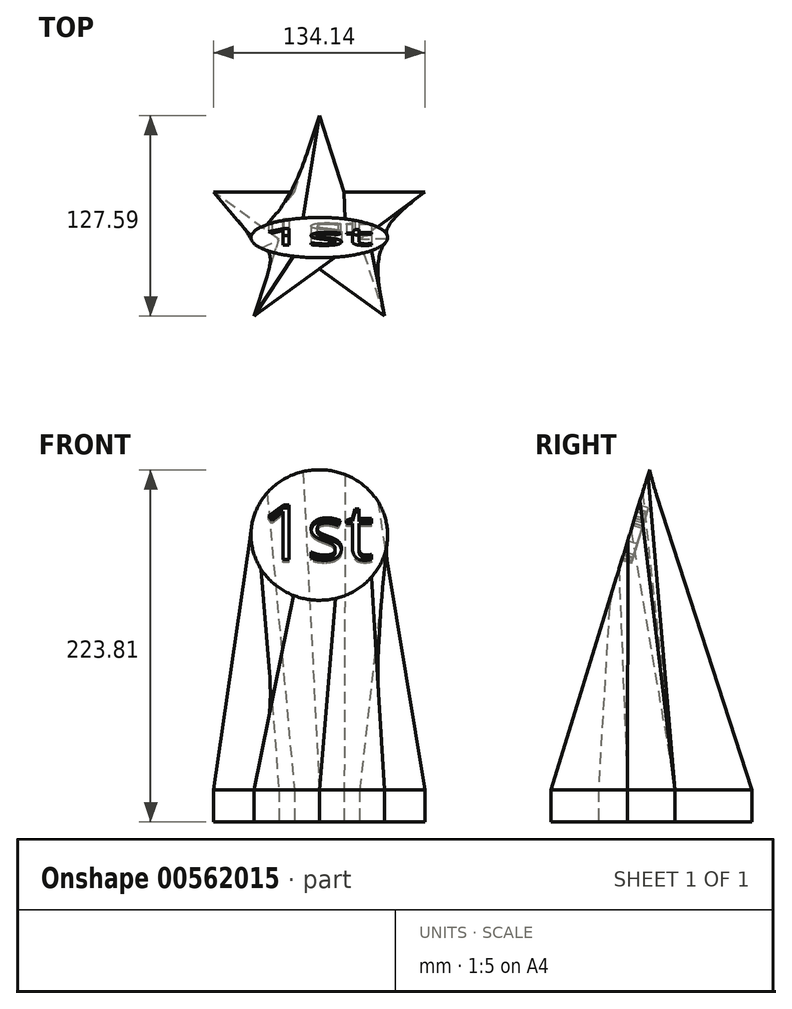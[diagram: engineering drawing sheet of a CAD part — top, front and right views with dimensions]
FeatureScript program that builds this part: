
annotation { "Feature Type Name" : "Feature", "Feature Type Description" : "" }
export const myFeature = defineFeature(function(context is Context, id is Id, definition is map)
    precondition{}
    {
        {
            var Q0;
            Q0=qCreatedBy(makeId("Top.planeOp"),FACE);
            var sketch = newSketch(context, id + "F0", { "sketchPlane" : qUnion([Q0])});
            skPoint(sketch, "E0.0.midPoint", {"position": v(-33.54, 46.16) * mm});
            skLineSegment(sketch, "E1", {"start": v(41.45, -57.06) * mm, "end": v(0, -26.94) * mm});
            skLineSegment(sketch, "E2", {"start": v(67.07, 21.8) * mm, "end": v(25.62, -8.32) * mm});
            skLineSegment(sketch, "E3", {"start": v(-41.45, -57.06) * mm, "end": v(-25.62, -8.32) * mm});
            skLineSegment(sketch, "E4", {"start": v(41.45, -57.06) * mm, "end": v(25.62, -8.32) * mm});
            skLineSegment(sketch, "E5", {"start": v(67.07, 21.8) * mm, "end": v(15.83, 21.8) * mm});
            skLineSegment(sketch, "E6.trimOffspring", {"start": v(-15.83, 21.8) * mm, "end": v(0, 70.53) * mm});
            skLineSegment(sketch, "E7.trimOffspring", {"start": v(-15.83, 21.8) * mm, "end": v(-67.07, 21.8) * mm});
            skLineSegment(sketch, "E8.trimOffspring", {"start": v(15.83, 21.8) * mm, "end": v(0, 70.53) * mm});
            skLineSegment(sketch, "E9.trimOffspring", {"start": v(0, -26.94) * mm, "end": v(-41.45, -57.06) * mm});
            skLineSegment(sketch, "E10.trimOffspring", {"start": v(-25.62, -8.32) * mm, "end": v(-67.07, 21.8) * mm});
            skLineSegment(sketch, "E11", {"start": v(-41.45, -57.06) * mm, "end": v(41.45, -57.06) * mm});
            skSolve(sketch);
        }
        {
            var Q0;
            Q0=makeQuery(id+"F0.imprint","IMPRINT",FACE,{"disambiguationData":[TD([[makeQuery(id+"F0.imprint","IMPRINT",EDGE,{"derivedFrom":sQuery(id+"F0.wireOp",EDGE,"E1")}),-1.0]])]});
            extrude(context, id + "F1", {"entities" : qUnion([Q0]), "depth" : 20.32 * mm, "offsetDistance" : 25.4 * mm});
        }
        {
            var Q0;
            Q0=makeQuery(id+"F1.opExtrude","CAP_FACE",FACE,{"disambiguationData":[OSD([sQuery(id+"F0.wireOp",EDGE,"E1"),sQuery(id+"F0.wireOp",EDGE,"E2"),sQuery(id+"F0.wireOp",EDGE,"E3"),sQuery(id+"F0.wireOp",EDGE,"E4"),sQuery(id+"F0.wireOp",EDGE,"E5"),sQuery(id+"F0.wireOp",EDGE,"E6.trimOffspring"),sQuery(id+"F0.wireOp",EDGE,"E7.trimOffspring"),sQuery(id+"F0.wireOp",EDGE,"E8.trimOffspring"),sQuery(id+"F0.wireOp",EDGE,"E9.trimOffspring"),sQuery(id+"F0.wireOp",EDGE,"E10.trimOffspring")])],"isStart":false});
            var sketch = newSketch(context, id + "F2", { "sketchPlane" : qUnion([Q0])});
            skLineSegment(sketch, "E12.0", {"start": v(-41.45, -57.06) * mm, "end": v(41.45, -57.06) * mm});
            skSolve(sketch);
        }
        {
            var Q0;
            Q0=sQuery(id+"F2.wireOp",EDGE,"E12.0");
            cPlane(context, id + "F3", {"entities" : qUnion([Q0]), "cplaneType" : CPlaneType.LINE_ANGLE, "offset" : 25.4 * mm, "angle" : 17.13 * degree, "oppositeDirection" : true, "width" : 152.4 * mm, "height" : 152.4 * mm});
        }
        {
            var Q0;
            Q0=qCreatedBy(id+"F3.planeOp",FACE);
            var sketch = newSketch(context, id + "F4", { "sketchPlane" : qUnion([Q0])});
            skCircle(sketch, "E13", {"center": v(0, 172.18) * mm, "radius": 43.38 * mm});
            skSolve(sketch);
        }
        {
            var Q1;
            Q1=makeQuery(id+"F4.imprint","IMPRINT",FACE,{"disambiguationData":[TD([[makeQuery(id+"F4.imprint","IMPRINT",EDGE,{"derivedFrom":sQuery(id+"F4.wireOp",EDGE,"E13")}),1.0]])]});
            var Q2;
            Q2=makeQuery(id+"F2.imprint","IMPRINT",FACE,{"disambiguationData":[TD([[makeQuery(id+"F2.imprint","IMPRINT",EDGE,{"derivedFrom":makeQuery(id+"F1.opExtrude","CAP_EDGE",EDGE,{"disambiguationData":[OSD([sQuery(id+"F0.wireOp",EDGE,"E1")])],"isStart":false})}),-1.0]])]});
            loft(context, id + "F5", {"operationType" : NewBodyOperationType.ADD, "sheetProfilesArray" : [{ "sheetProfileEntities" : qUnion([Q1]) }, { "sheetProfileEntities" : qUnion([Q2]) }]});
        }
        {
            var Q0;
            Q0=makeQuery(id+"F5.opLoft","CAP_FACE",FACE,{"disambiguationData":[OSD([makeQuery(id+"F4.imprint","IMPRINT",FACE,{"disambiguationData":[TD([[makeQuery(id+"F4.imprint","IMPRINT",EDGE,{"derivedFrom":sQuery(id+"F4.wireOp",EDGE,"E13")}),1.0]])]})])],"isStart":true});
            var sketch = newSketch(context, id + "F6", { "sketchPlane" : qUnion([Q0])});
            skText(sketch, "E14", { "text": "1st", "fontName": "OpenSans-Regular.ttf"});
            const initialGuessF6  = {"E14": [-0.0369, 0.15586, 1, 0, 0.03659]};
            skSetInitialGuess(sketch, initialGuessF6);
            skSolve(sketch);
        }
        {
            var Q0;
            Q0 = qSketchRegion(id + "F6", true);
            extrude(context, id + "F7", {"entities" : qUnion([Q0]), "operationType" : NewBodyOperationType.REMOVE, "oppositeDirection" : true, "depth" : 6.35 * mm, "offsetDistance" : 25.4 * mm});
        }
    });
